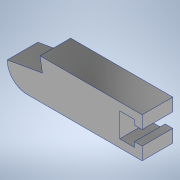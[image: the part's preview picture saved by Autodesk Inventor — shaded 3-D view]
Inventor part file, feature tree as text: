
AUTODESK INVENTOR PART (.ipt)
format: ipt  version: 2022 (Build 260153000, 153)  size: 146,944 bytes
history: native  units: mm
features: extrude x2, sketch x2
ambient origin geometry x8: Origin, YZ Plane, XZ Plane, XY Plane, X Axis, Y Axis, Z Axis, Center Point
bodies: Body1 (feature_tree)
feature tree (4):
  extrude  "Extrusion2"  Depth=5.8mm
  extrude  "Extrusion5"  Depth=12.0mm TaperAngle=0.0deg
  sketch  "Sketch5"  dims[d41=5.8mm d48=44.0mm]
  sketch  "Sketch8"  dims[d50=3.0mm d56=12.0mm d57=0.0mm d63=45.0mm d67=15.6mm d71=0.0mm d72=36.2mm d80=17.453293mm d81=1.745329mm d82=0.0mm d83=0.0mm d87=5.6mm d88=9.5mm d89=14.0mm]
